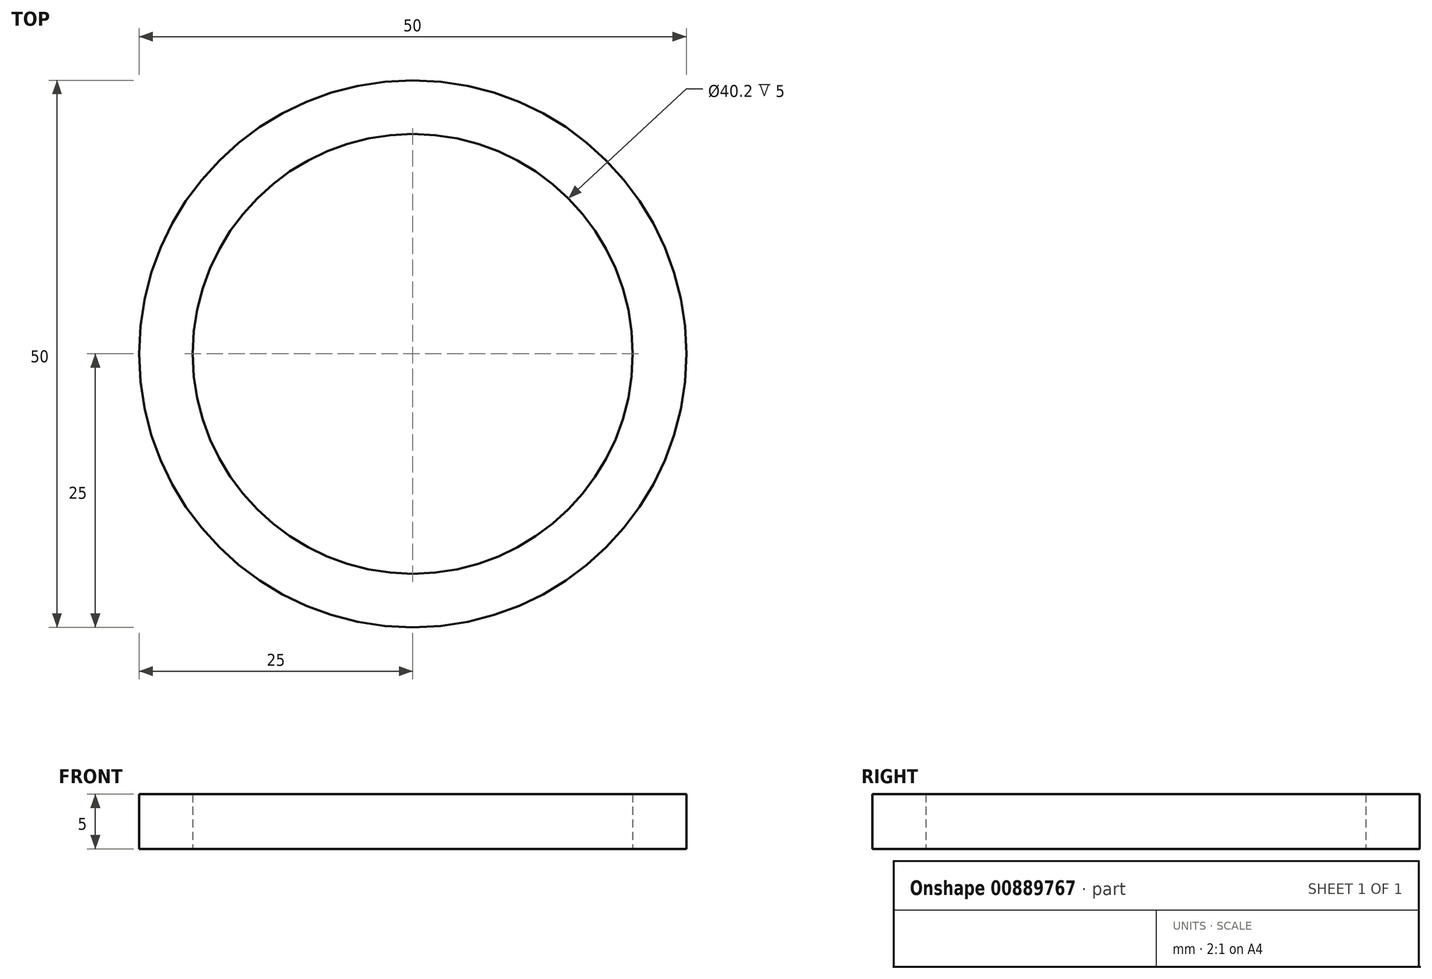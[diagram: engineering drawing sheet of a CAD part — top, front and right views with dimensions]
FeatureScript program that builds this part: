
annotation { "Feature Type Name" : "Feature", "Feature Type Description" : "" }
export const myFeature = defineFeature(function(context is Context, id is Id, definition is map)
    precondition{}
    {
        {
            var Q0;
            Q0=qCreatedBy(makeId("Top.planeOp"),FACE);
            var sketch = newSketch(context, id + "F0", { "sketchPlane" : qUnion([Q0])});
            skCircle(sketch, "E0", {"center": v(0, 0) * mm, "radius": 25 * mm});
            skCircle(sketch, "E1", {"center": v(0, 0) * mm, "radius": 20.1 * mm});
            skFitSpline(sketch, "E2", {"points": [v(17.97, 4.6) * mm, v(7.83, 74.33) * mm], "startDerivative": vector(-10.14, 69.72) * mm, "endDerivative": vector(-10.14, 69.72) * mm});
            skSolve(sketch);
        }
        {
            var Q0;
            Q0=makeQuery(id+"F0.imprint","IMPRINT",FACE,{"disambiguationData":[TD([[makeQuery(id+"F0.imprint","IMPRINT",EDGE,{"derivedFrom":sQuery(id+"F0.wireOp",EDGE,"E0")}),1.0]])]});
            var sketch = newSketch(context, id + "F1", { "sketchPlane" : qUnion([Q0])});
            skSolve(sketch);
        }
        {
            var Q0;
            Q0 = qSketchRegion(id + "F1", true);
            var Q1;
            Q1=makeQuery(id+"F1.imprint","IMPRINT",FACE,{"disambiguationData":[TD([[makeQuery(id+"F1.imprint","IMPRINT",EDGE,{"derivedFrom":makeQuery(id+"F0.imprint","IMPRINT",EDGE,{"derivedFrom":sQuery(id+"F0.wireOp",EDGE,"E0")})}),1.0]])]});
            extrude(context, id + "F2", {"entities" : qUnion([Q0, Q1]), "depth" : 5 * mm, "offsetDistance" : 25.4 * mm});
        }
    });
